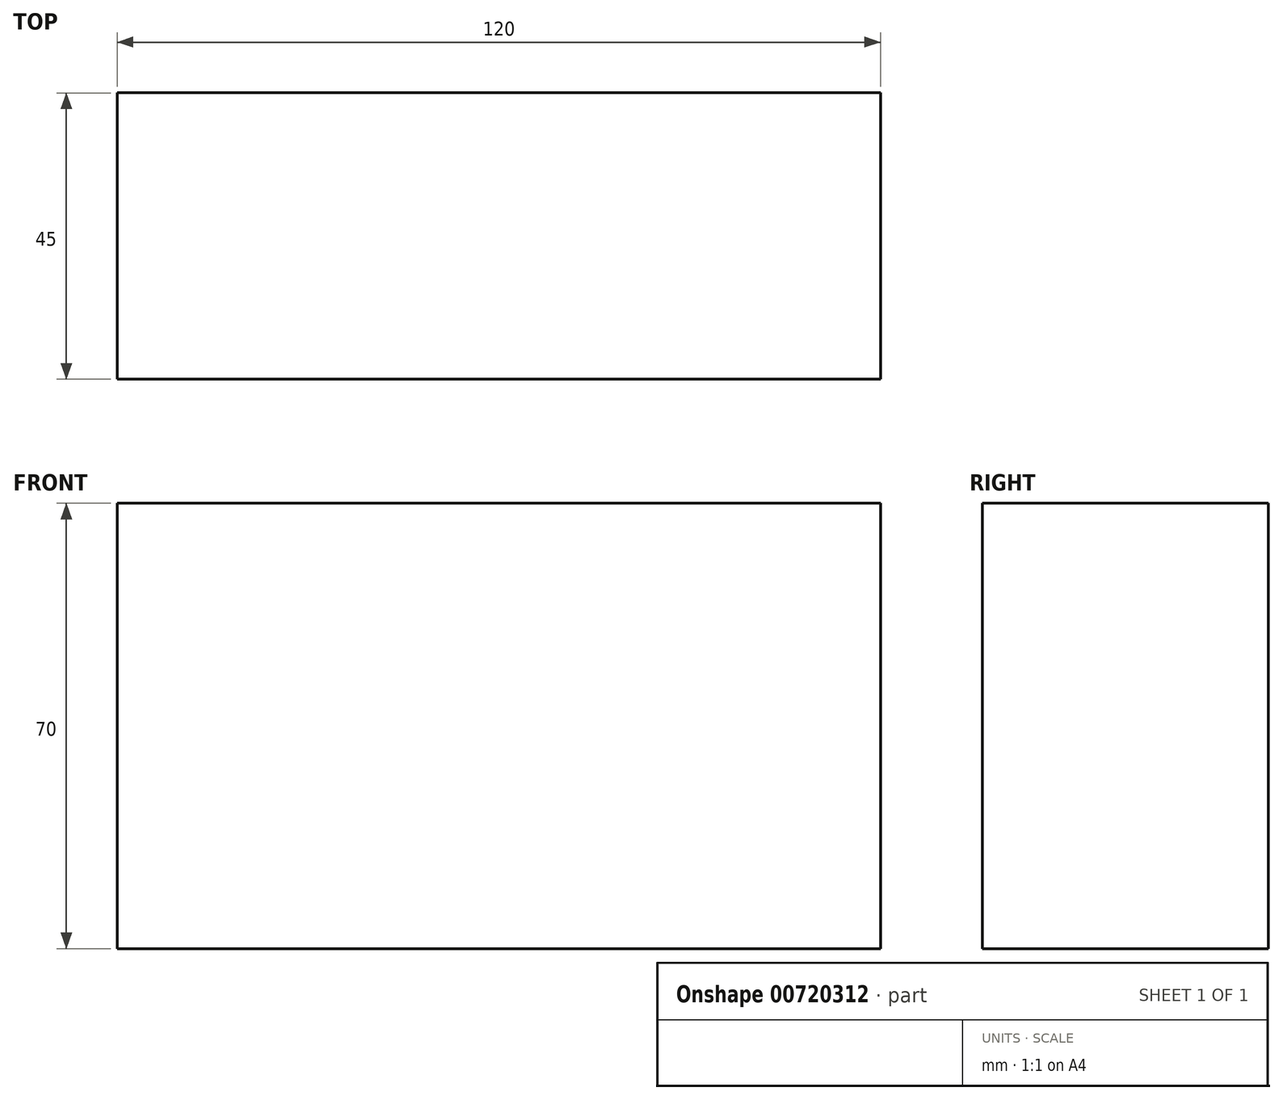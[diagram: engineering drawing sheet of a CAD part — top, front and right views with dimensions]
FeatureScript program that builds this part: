
annotation { "Feature Type Name" : "Feature", "Feature Type Description" : "" }
export const myFeature = defineFeature(function(context is Context, id is Id, definition is map)
    precondition{}
    {
        {
            var Q0;
            Q0=qCreatedBy(makeId("Top.planeOp"),FACE);
            var sketch = newSketch(context, id + "F0", { "sketchPlane" : qUnion([Q0])});
            skLineSegment(sketch, "E0.bottom", {"start": v(-52.51, 20.31) * mm, "end": v(67.49, 20.31) * mm});
            skLineSegment(sketch, "E0.top", {"start": v(-52.51, -24.69) * mm, "end": v(67.49, -24.69) * mm});
            skLineSegment(sketch, "E0.left", {"start": v(-52.51, 20.31) * mm, "end": v(-52.51, -24.69) * mm});
            skLineSegment(sketch, "E0.right", {"start": v(67.49, 20.31) * mm, "end": v(67.49, -24.69) * mm});
            skSolve(sketch);
        }
        {
            var Q0;
            Q0=makeQuery(id+"F0.imprint","IMPRINT",FACE,{"disambiguationData":[TD([[makeQuery(id+"F0.imprint","IMPRINT",EDGE,{"derivedFrom":sQuery(id+"F0.wireOp",EDGE,"E0.bottom")}),-1.0]])]});
            extrude(context, id + "F1", {"entities" : qUnion([Q0]), "depth" : 70 * mm, "offsetDistance" : 25 * mm});
        }
    });
